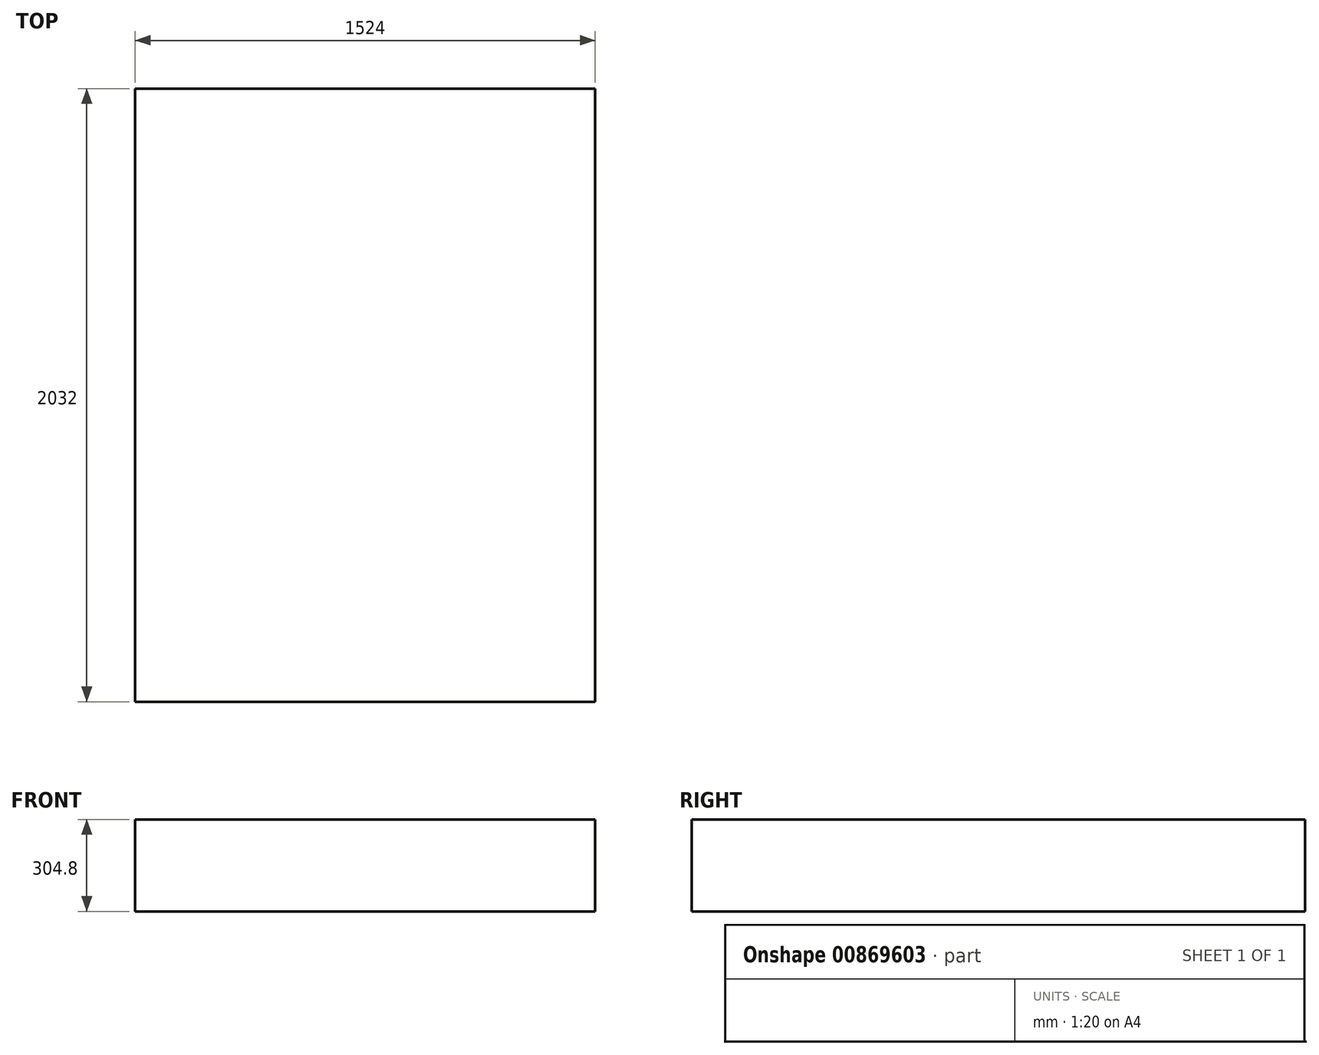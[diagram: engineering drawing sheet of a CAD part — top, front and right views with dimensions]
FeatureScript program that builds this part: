
annotation { "Feature Type Name" : "Feature", "Feature Type Description" : "" }
export const myFeature = defineFeature(function(context is Context, id is Id, definition is map)
    precondition{}
    {
        {
            var Q0;
            Q0=qCreatedBy(makeId("Top.planeOp"),FACE);
            var sketch = newSketch(context, id + "F0", { "sketchPlane" : qUnion([Q0])});
            skLineSegment(sketch, "E0.bottom", {"start": v(3.28, 0) * mm, "end": v(1527.28, 0) * mm});
            skLineSegment(sketch, "E0.top", {"start": v(3.28, -2032) * mm, "end": v(1527.28, -2032) * mm});
            skLineSegment(sketch, "E0.left", {"start": v(3.28, 0) * mm, "end": v(3.28, -2032) * mm});
            skLineSegment(sketch, "E0.right", {"start": v(1527.28, 0) * mm, "end": v(1527.28, -2032) * mm});
            skSolve(sketch);
        }
        {
            var Q0;
            Q0 = qSketchRegion(id + "F0", true);
            extrude(context, id + "F1", {"entities" : qUnion([Q0]), "depth" : 304.8 * mm, "offsetDistance" : 25.4 * mm});
        }
    });
